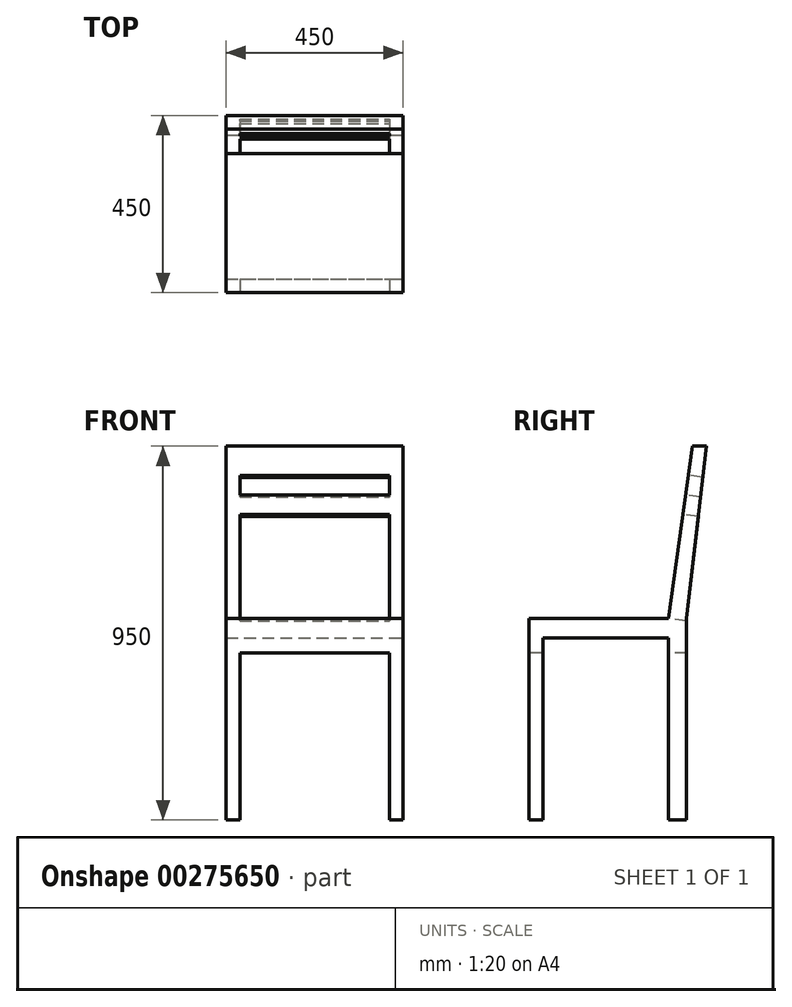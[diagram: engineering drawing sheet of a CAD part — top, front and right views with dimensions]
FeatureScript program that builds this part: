
annotation { "Feature Type Name" : "Feature", "Feature Type Description" : "" }
export const myFeature = defineFeature(function(context is Context, id is Id, definition is map)
    precondition{}
    {
        {
            var Q0;
            Q0=qCreatedBy(makeId("Top.planeOp"),FACE);
            var sketch = newSketch(context, id + "F0", { "sketchPlane" : qUnion([Q0])});
            skLineSegment(sketch, "E0.bottom", {"start": v(225, 225) * mm, "end": v(-225, 225) * mm});
            skLineSegment(sketch, "E0.top", {"start": v(225, -225) * mm, "end": v(-225, -225) * mm});
            skLineSegment(sketch, "E0.left", {"start": v(225, 225) * mm, "end": v(225, -225) * mm});
            skLineSegment(sketch, "E0.right", {"start": v(-225, 225) * mm, "end": v(-225, -225) * mm});
            skPoint(sketch, "E0.middle", {"position": v(0, 0) * mm});
            skSolve(sketch);
        }
        {
            var Q0;
            Q0=qSketchRegion(id+"F0",true);
            extrude(context, id + "F1", {"entities" : qUnion([Q0]), "depth" : 950 * mm});
        }
        {
            var Q0;
            Q0=makeQuery(id+"F1.opExtrude","SWEPT_FACE",FACE,{"disambiguationData":[OSD([sQuery(id+"F0.wireOp",EDGE,"E0.left")])]});
            var sketch = newSketch(context, id + "F2", { "sketchPlane" : qUnion([Q0])});
            skLineSegment(sketch, "E1.bottom", {"start": v(225, 462) * mm, "end": v(-225, 462) * mm});
            skLineSegment(sketch, "E1.top", {"start": v(225, 512) * mm, "end": v(-225, 512) * mm});
            skLineSegment(sketch, "E1.left", {"start": v(225, 462) * mm, "end": v(225, 512) * mm});
            skLineSegment(sketch, "E1.right", {"start": v(-225, 462) * mm, "end": v(-225, 512) * mm});
            skLineSegment(sketch, "E2", {"start": v(225, 950) * mm, "end": v(175, 512) * mm});
            skLineSegment(sketch, "E3", {"start": v(190, 950) * mm, "end": v(128.3, 512) * mm});
            skLineSegment(sketch, "E4", {"start": v(175, 512) * mm, "end": v(175, 0) * mm});
            skLineSegment(sketch, "E5", {"start": v(128.3, 512) * mm, "end": v(128.3, 0) * mm});
            skLineSegment(sketch, "E6", {"start": v(-190, 462) * mm, "end": v(-190, 0) * mm});
            skSolve(sketch);
        }
        {
            var Q0;
            {var subQ0=sQuery(id+"F2.wireOp",EDGE,"E1.left");Q0=makeQuery(id+"F2.imprint","IMPRINT",FACE,{"disambiguationData":[TD([[makeQuery(id+"F2.imprint","IMPRINT",EDGE,{"derivedFrom":subQ0}),-1.0]])]});}
            var Q1;
            {var subQ4=sQuery(id+"F2.wireOp",EDGE,"E3");Q1=makeQuery(id+"F2.imprint","IMPRINT",FACE,{"disambiguationData":[TD([[makeQuery(id+"F2.imprint","IMPRINT",EDGE,{"derivedFrom":subQ4}),-1.0]])]});}
            var Q2;
            {var subQ4=sQuery(id+"F2.wireOp",EDGE,"E2");Q2=makeQuery(id+"F2.imprint","IMPRINT",FACE,{"disambiguationData":[TD([[makeQuery(id+"F2.imprint","IMPRINT",EDGE,{"derivedFrom":subQ4}),1.0]])]});}
            var Q3;
            {var subQ1=sQuery(id+"F0.wireOp",EDGE,"E0.left");var subQ4=sQuery(id+"F2.wireOp",EDGE,"E4");var subQ6=makeQuery(id+"F1.opExtrude","CAP_EDGE",EDGE,{"disambiguationData":[OSD([subQ1])],"isStart":true});var subQ8=makeQuery(id+"F2.imprint","INTERSECT",VERTEX,{"derivedFrom":[subQ6,subQ4]});Q3=makeQuery(id+"F2.imprint","IMPRINT",FACE,{"disambiguationData":[TD([[makeQuery(id+"F2.imprint","IMPRINT",EDGE,{"disambiguationData":[TD([[subQ8,1.0]])],"derivedFrom":subQ4}),1.0]])]});}
            var Q4;
            {var subQ0=sQuery(id+"F2.wireOp",EDGE,"E6");Q4=makeQuery(id+"F2.imprint","IMPRINT",FACE,{"disambiguationData":[TD([[makeQuery(id+"F2.imprint","IMPRINT",EDGE,{"derivedFrom":subQ0}),1.0]])]});}
            extrude(context, id + "F3", {"entities" : qUnion([Q0, Q1, Q2, Q3, Q4]), "operationType" : NewBodyOperationType.REMOVE, "endBound" : BoundingType.THROUGH_ALL, "oppositeDirection" : true, "depth" : 25 * mm});
        }
        {
            var Q0;
            Q0=makeQuery(id+"F1.opExtrude","SWEPT_FACE",FACE,{"disambiguationData":[OSD([sQuery(id+"F0.wireOp",EDGE,"E0.top")])]});
            var sketch = newSketch(context, id + "F4", { "sketchPlane" : qUnion([Q0])});
            skLineSegment(sketch, "E7", {"start": v(-190, 0) * mm, "end": v(-190, 425) * mm});
            skLineSegment(sketch, "E8", {"start": v(-190, 425) * mm, "end": v(190, 425) * mm});
            skLineSegment(sketch, "E9", {"start": v(190, 425) * mm, "end": v(190, 0) * mm});
            skSolve(sketch);
        }
        {
            var Q0;
            Q0 = qSketchRegion(id + "F4", true);
            var Q1;
            {var subQ0=sQuery(id+"F4.wireOp",EDGE,"E7");Q1=makeQuery(id+"F4.imprint","IMPRINT",FACE,{"disambiguationData":[TD([[makeQuery(id+"F4.imprint","IMPRINT",EDGE,{"derivedFrom":subQ0}),-1.0]])]});}
            extrude(context, id + "F5", {"entities" : qUnion([Q0, Q1]), "operationType" : NewBodyOperationType.REMOVE, "endBound" : BoundingType.THROUGH_ALL, "oppositeDirection" : true, "depth" : 25 * mm});
        }
        {
            var Q0;
            Q0=makeQuery(id+"F3.boolean.opBoolean","COPY",FACE,{"derivedFrom":makeQuery(id+"F3.opExtrude","SWEPT_FACE",FACE,{"disambiguationData":[OSD([sQuery(id+"F2.wireOp",EDGE,"E3")])]})});
            var sketch = newSketch(context, id + "F6", { "sketchPlane" : qUnion([Q0])});
            skLineSegment(sketch, "E10", {"start": v(-190, 524.9) * mm, "end": v(-190, 892.22) * mm});
            skLineSegment(sketch, "E11", {"start": v(-190, 892.22) * mm, "end": v(190, 892.22) * mm});
            skLineSegment(sketch, "E12", {"start": v(190, 892.22) * mm, "end": v(190, 524.9) * mm});
            skLineSegment(sketch, "E13", {"start": v(-190, 842.22) * mm, "end": v(190, 842.22) * mm});
            skLineSegment(sketch, "E14", {"start": v(-190, 792.22) * mm, "end": v(190, 792.22) * mm});
            skSolve(sketch);
        }
        {
            var Q0;
            {var subQ3=sQuery(id+"F6.wireOp",EDGE,"E14");Q0=makeQuery(id+"F6.imprint","IMPRINT",FACE,{"disambiguationData":[TD([[makeQuery(id+"F6.imprint","IMPRINT",EDGE,{"derivedFrom":subQ3}),-1.0]])]});}
            var Q1;
            {var subQ0=sQuery(id+"F6.wireOp",EDGE,"E11");Q1=makeQuery(id+"F6.imprint","IMPRINT",FACE,{"disambiguationData":[TD([[makeQuery(id+"F6.imprint","IMPRINT",EDGE,{"derivedFrom":subQ0}),-1.0]])]});}
            extrude(context, id + "F7", {"entities" : qUnion([Q0, Q1]), "operationType" : NewBodyOperationType.REMOVE, "endBound" : BoundingType.THROUGH_ALL, "oppositeDirection" : true, "depth" : 25 * mm});
        }
    });
